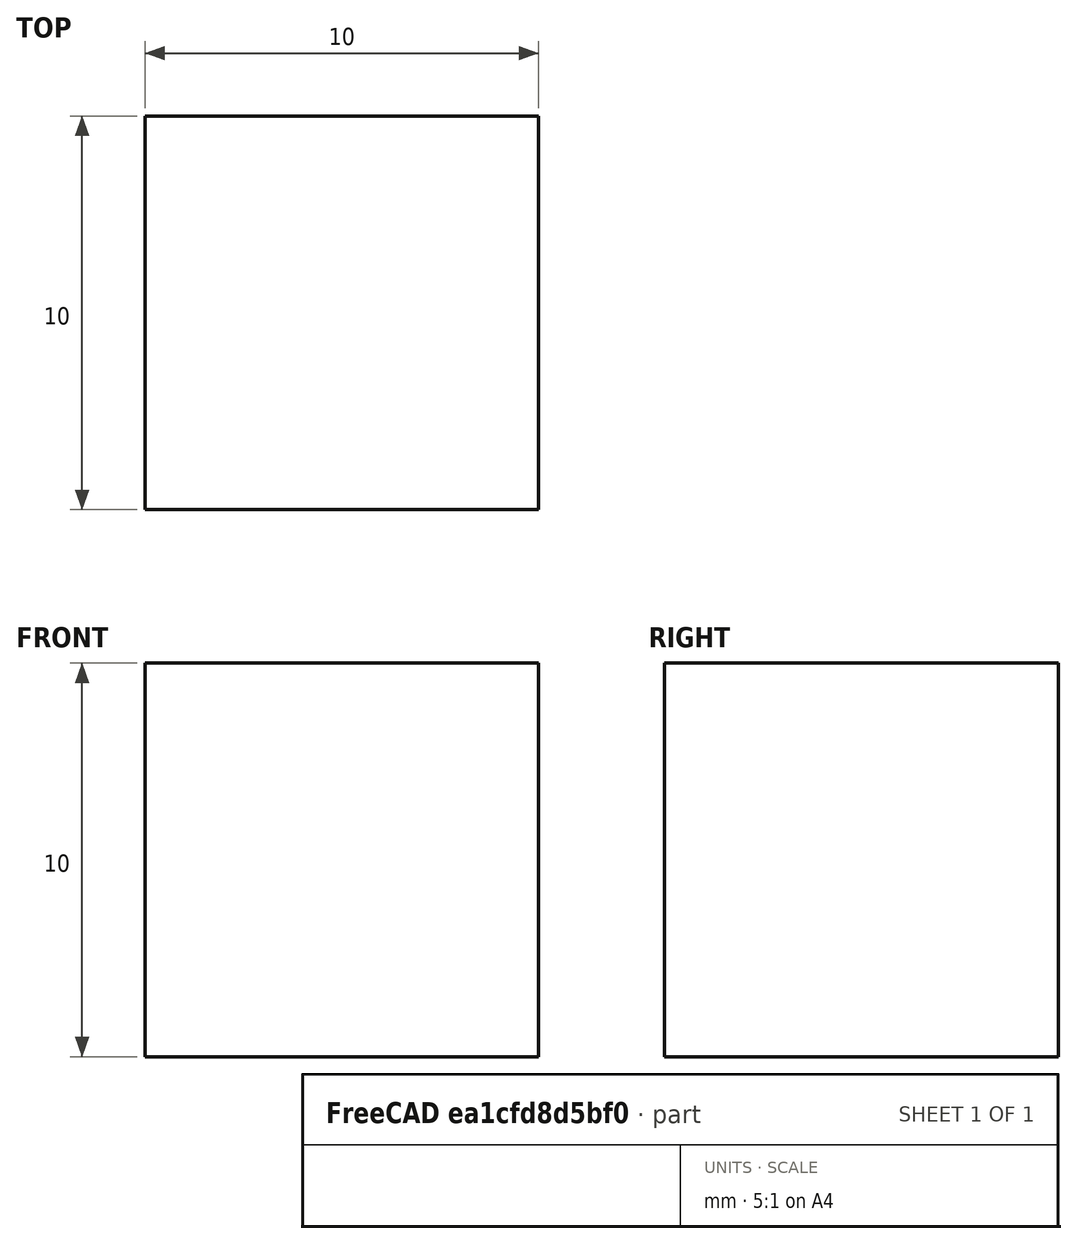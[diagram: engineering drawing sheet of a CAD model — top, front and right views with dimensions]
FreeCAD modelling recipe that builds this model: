
FCSTD DOCUMENT  (FreeCAD 0.17R11473 (Git))
Label: test_project
License: All rights reserved
LicenseURL: http://en.wikipedia.org/wiki/All_rights_reserved
objects: Path::FeaturePython×3, Part::Box×1, Path::FeatureCompoundPython×1
note: 2 computed .brp shape members not serialized (recipe doc carries the construction recipe); baked Part::Feature solids carry a one-line shape summary decoded from their .brp

FEATURE [Part::Box] Box  label="Cube"
  AttacherType = Attacher::AttachEngine3D
  Height = 10
  Length = 10
  Width = 10
FEATURE [Path::FeaturePython] Default_Tool  # Path/CAM operation (typed FeaturePython)
  HorizFeed = 0
  HorizRapid = 0
  SpindleDir = 0
  SpindleSpeed = 0
  ToolNumber = 2
  VertFeed = 0
  VertRapid = 0
FEATURE [Path::FeaturePython] Contour  # Path/CAM operation (typed FeaturePython)
  Active = true
  AreaParams:
    OpenMode = 0
    Angle = 45.0
    MinArcPoints = 4
    Coplanar = 2
    Tolerance = 1e-07
    CleanDistance = 0.0
    PocketExtraOffset = 0.0
    AngleShift = 0.0
    SubjectFill = 0
    RoundPreceision = 0.0
    Simplify = False
    SectionTolerance = 1e-06
    MaxArcPoints = 100
    SectionOffset = 0.0
    Offset = 0.0
    Accuracy = 0.01
    PocketStepover = 0.0
    ClipFill = 0
    ToolRadius = 1.0
    Outline = False
    ClipperScale = 10000000.0
    FromCenter = True
    Explode = False
    EndType = 0
    Shift = 0.0
    ExtraPass = 0
    Project = False
    JoinType = 0
    Thicken = False
    Stepdown = 1.0
    SectionMode = 2
    MiterLimit = 2.0
    Deflection = 0.01
    Reorient = True
    FitArcs = True
    SectionCount = 0
    PocketMode = 0
    Stepover = 0.0
    Unit = 1.0
    Fill = 0
  ClearanceHeight = 15
  Direction = 0
  FinalDepth = 0
  OffsetExtra = 0
  PathParams = {'resume_height': 1.0, 'feedrate': 0.0, 'verbose': True, 'orientation': 0, 'return_end': True, 'shapes': [<Compound object at 0x3f1ec30>, <Compound object at 0x3925c20>, <Compound object at 0x3f13540>, <Compound object at 0x3f0c9f0>, <Compound object at 0x3f1b220>, <Compound object at 0x3f1ca20>, <Compound object at 0x3f0d920>, <Compound object at 0x3f17f20>, <Compound object at 0x3f195c0>, <Compound object at 0x3f23540>], 'start': Vector (0.0, 0.0, 0.0), 'retraction': 15.0, 'feedrate_v': 0.0}
  SafeHeight = 12
  StartDepth = 10
  StartPoint = (0,0,0)
  StepDown = 1
  ToolController = -> Default_Tool
  UseComp = false
FEATURE [Path::FeaturePython] T1__Default_Tool  # Path/CAM operation (typed FeaturePython)
  HorizFeed = 0
  HorizRapid = 0
  SpindleDir = 0
  SpindleSpeed = 0
  ToolNumber = 1
  VertFeed = 0
  VertRapid = 0
FEATURE [Path::FeatureCompoundPython] Job  # Path/CAM operation (typed FeaturePython)
  Base = -> Box
  GeometryTolerance = 0.01
  Group = -> [Default_Tool,Contour,T1__Default_Tool]
  PostProcessor = 4
  PostProcessorArgs = --no-header --no-line-numbers --no-comments --no-show-editor --output-precision=2
  UsePlacements = false
